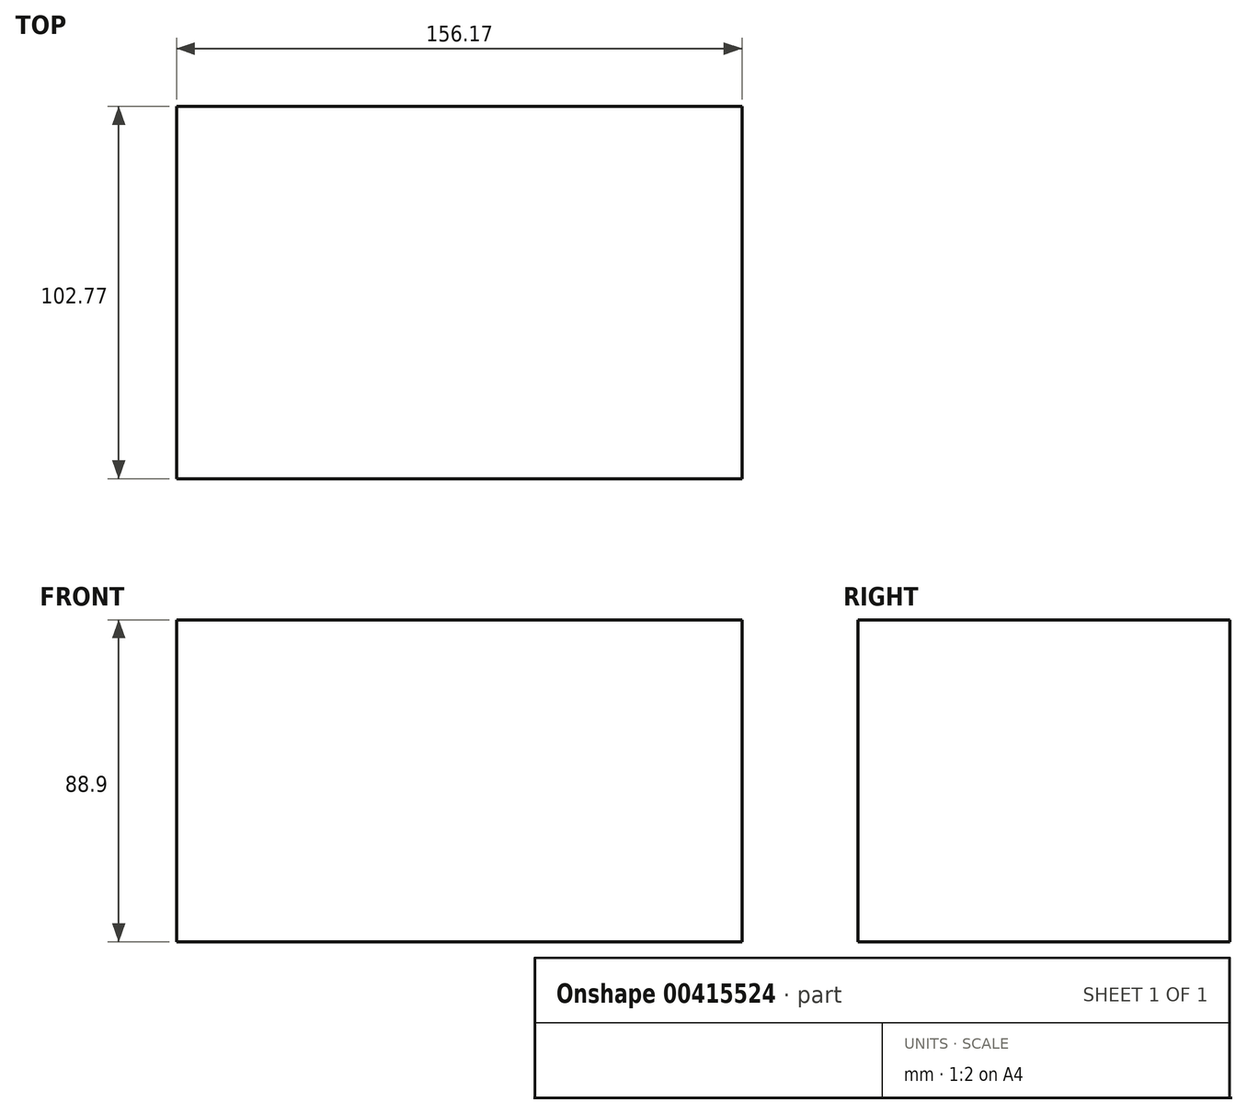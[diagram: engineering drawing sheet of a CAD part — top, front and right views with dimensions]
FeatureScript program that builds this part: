
annotation { "Feature Type Name" : "Feature", "Feature Type Description" : "" }
export const myFeature = defineFeature(function(context is Context, id is Id, definition is map)
    precondition{}
    {
        {
            var Q0;
            Q0=qCreatedBy(makeId("Top.planeOp"),FACE);
            var sketch = newSketch(context, id + "F0", { "sketchPlane" : qUnion([Q0])});
            skLineSegment(sketch, "E0.bottom", {"start": v(77.96, -53.77) * mm, "end": v(-78.21, -53.77) * mm});
            skLineSegment(sketch, "E0.top", {"start": v(77.96, 49) * mm, "end": v(-78.21, 49) * mm});
            skLineSegment(sketch, "E0.left", {"start": v(77.96, -53.77) * mm, "end": v(77.96, 49) * mm});
            skLineSegment(sketch, "E0.right", {"start": v(-78.21, -53.77) * mm, "end": v(-78.21, 49) * mm});
            skSolve(sketch);
        }
        {
            var Q0;
            Q0 = qSketchRegion(id + "F0", true);
            extrude(context, id + "F1", {"entities" : qUnion([Q0]), "depth" : 88.9 * mm});
        }
    });
